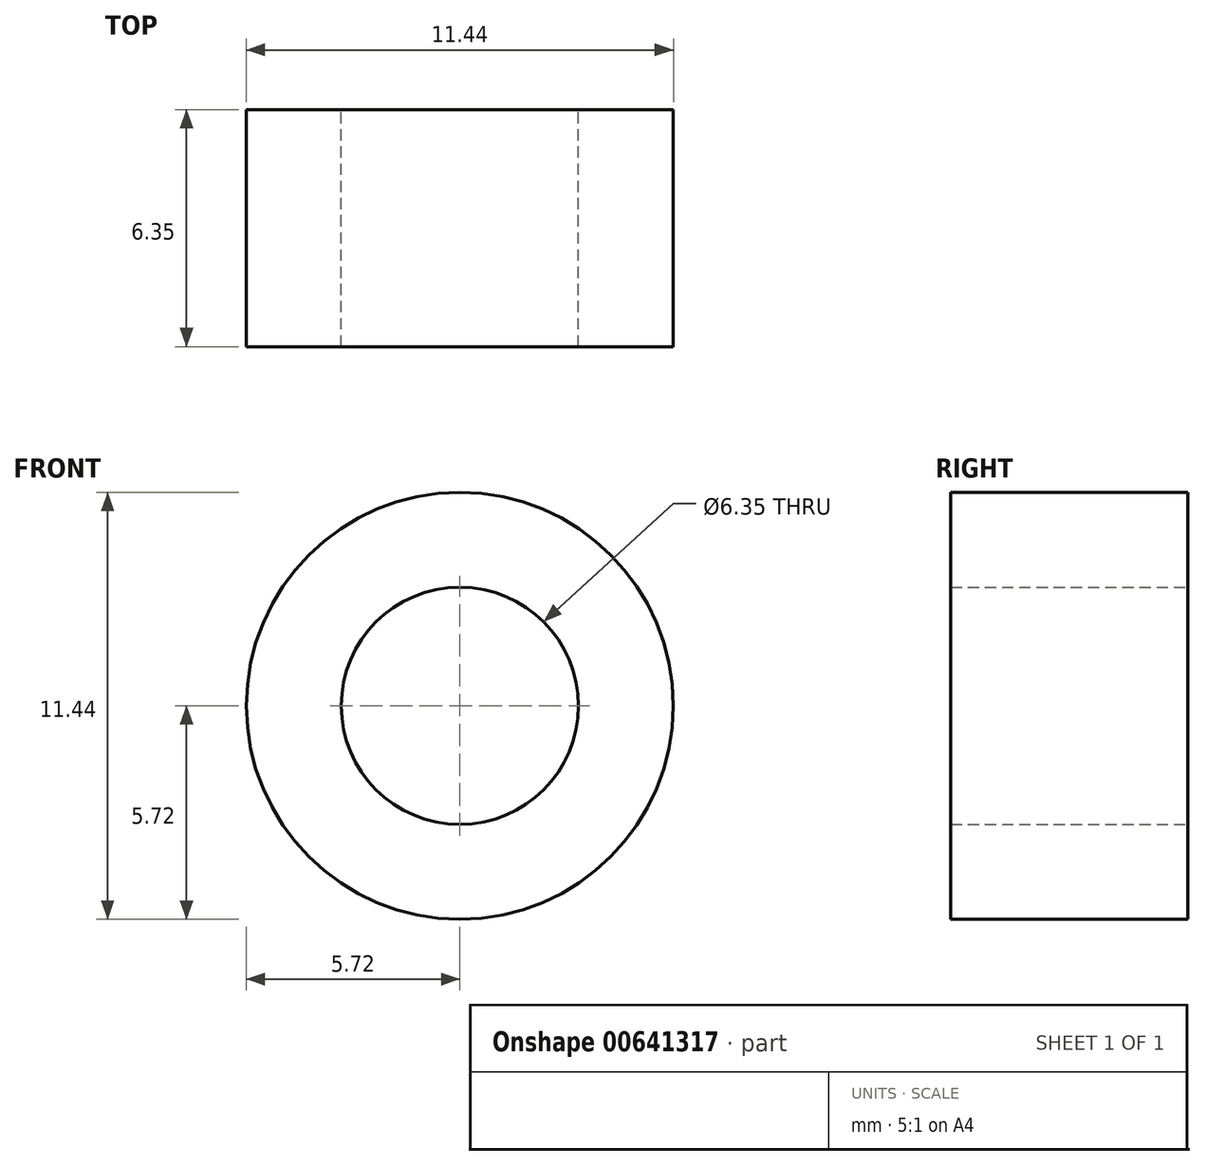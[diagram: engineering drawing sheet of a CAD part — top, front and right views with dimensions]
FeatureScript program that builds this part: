
annotation { "Feature Type Name" : "Feature", "Feature Type Description" : "" }
export const myFeature = defineFeature(function(context is Context, id is Id, definition is map)
    precondition{}
    {
        {
            var Q0;
            Q0=qCreatedBy(makeId("Front.planeOp"),FACE);
            var sketch = newSketch(context, id + "F0", { "sketchPlane" : qUnion([Q0])});
            skCircle(sketch, "E0", {"center": v(0, 0) * mm, "radius": 5.72 * mm});
            skCircle(sketch, "E1", {"center": v(0, 0) * mm, "radius": 3.18 * mm});
            skSolve(sketch);
        }
        {
            var Q0;
            Q0=makeQuery(id+"F0.imprint","IMPRINT",FACE,{"disambiguationData":[TD([[makeQuery(id+"F0.imprint","IMPRINT",EDGE,{"derivedFrom":sQuery(id+"F0.wireOp",EDGE,"E0")}),1.0]])]});
            extrude(context, id + "F1", {"entities" : qUnion([Q0]), "depth" : 6.35 * mm, "offsetDistance" : 25.4 * mm});
        }
    });
